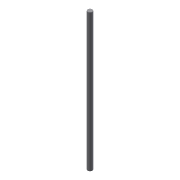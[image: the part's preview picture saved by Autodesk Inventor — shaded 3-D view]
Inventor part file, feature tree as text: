
AUTODESK INVENTOR PART (.ipt)
format: ipt  version: 2019.4 (Build 234330000, 330)  size: 68,096 bytes
history: native  units: mm
features: extrude x1, sketch x1
ambient origin geometry x8: Origin, YZ Plane, XZ Plane, XY Plane, X Axis, Y Axis, Z Axis, Center Point
bodies: Solid1 (feature_tree)
feature tree (2):
  extrude  "Extrusion1"  Depth=180.0mm TaperAngle=0.0deg
  sketch  "Sketch1"  dims[d0=6.0mm d1=180.0mm d2=0.0mm]
